FCSTD DOCUMENT  (FreeCAD 0.19R24276 (Git))
Label: Round_knife
License: All rights reserved
LicenseURL: http://en.wikipedia.org/wiki/All_rights_reserved
objects: Sketcher::SketchObject×1, PartDesign::Body×1
note: 2 computed .brp shape members not serialized (recipe doc carries the construction recipe); baked Part::Feature solids carry a one-line shape summary decoded from their .brp

FEATURE [Sketcher::SketchObject] Sketch
  FullyConstrained = false
  MapMode = 5
  Support = -> [XY_Plane]
  sketch-geometry (5):
    g0: LineSegment StartX=33.4953 StartY=-8.20608 StartZ=0 EndX=39.2892 EndY=11.9788 EndZ=0
    g1: LineSegment StartX=48.9928 StartY=14.3954 StartZ=0 EndX=43.1989 EndY=-5.78953 EndZ=0
    g2: LineSegment StartX=33.4953 StartY=-8.20608 StartZ=0 EndX=43.1989 EndY=-5.78953 EndZ=0
    g3: LineSegment StartX=39.2892 StartY=11.9788 StartZ=0 EndX=48.9928 EndY=14.3954 EndZ=0
    g4: LineSegment StartX=38.7374 StartY=10.0565 StartZ=0 EndX=48.441 EndY=12.473 EndZ=0
  constraints (12):
    c: Parallel(g0,g1)
    c: Coincident(g2,g0)
    c: Coincident(g2,g1)
    c: Coincident(g3,g0)
    c: Coincident(g3,g1)
    c: Angle(g2,g0) = 1.0472
    c: Parallel(g2,g3)
    c: Distance(g0,g1) = 10
    c: PointOnObject(g4,g0)
    c: PointOnObject(g4,g1)
    c: Parallel(g4,g3)
    c: Distance(g4,g0) = 2
FEATURE [PartDesign::Body] Body
  Group = -> [Sketch]
  Origin = -> Origin
